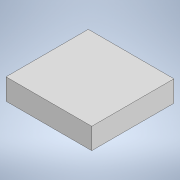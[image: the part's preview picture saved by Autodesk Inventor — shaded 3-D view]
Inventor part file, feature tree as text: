
AUTODESK INVENTOR PART (.ipt)
format: ipt  version: 2020 (Build 240168000, 168)  size: 90,624 bytes
history: native  units: mm
features: other x1, extrude x1, sketch x1
ambient origin geometry x8: Origin, YZ Plane, XZ Plane, XY Plane, X Axis, Y Axis, Z Axis, Center Point
bodies: Body1 (feature_tree)
feature tree (3):
  other  "Bryła1"
  extrude  "Wyciągnięcie proste1"  Depth=75.0mm
  sketch  "Szkic1"
